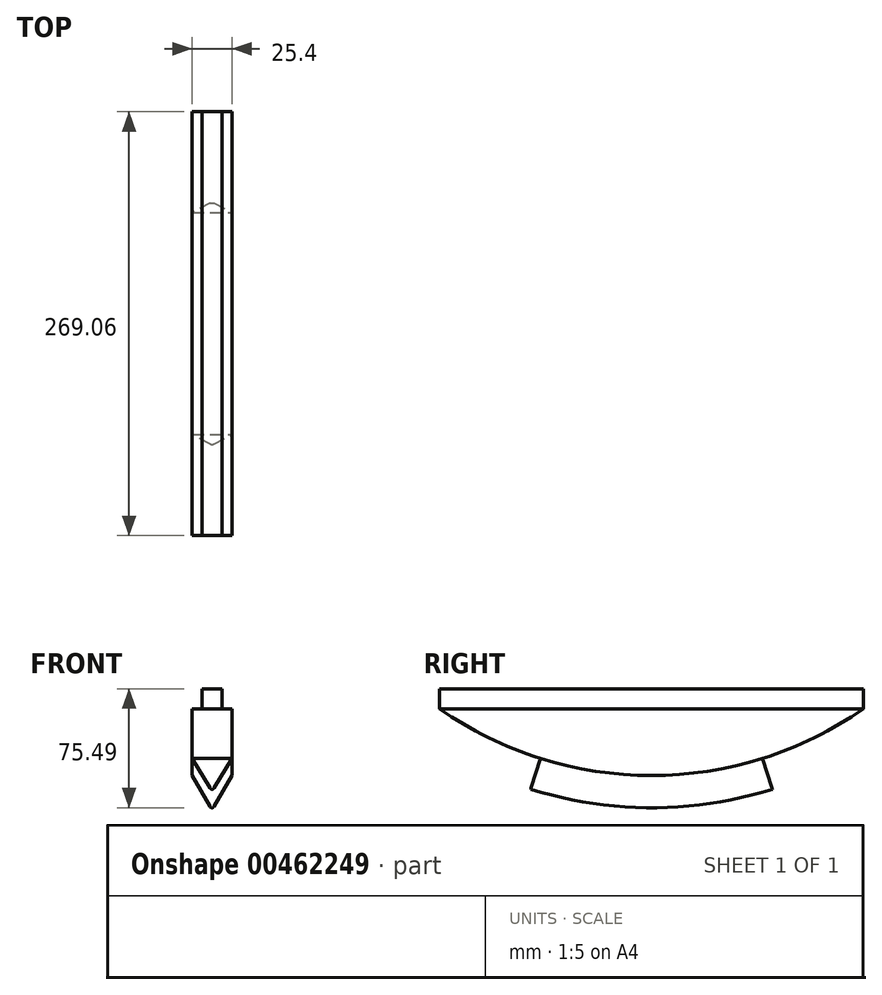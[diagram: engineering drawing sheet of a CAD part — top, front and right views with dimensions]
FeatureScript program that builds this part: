
annotation { "Feature Type Name" : "Feature", "Feature Type Description" : "" }
export const myFeature = defineFeature(function(context is Context, id is Id, definition is map)
    precondition{}
    {
        {
            var Q0;
            Q0=qCreatedBy(makeId("Front.planeOp"),FACE);
            var sketch = newSketch(context, id + "F0", { "sketchPlane" : qUnion([Q0])});
            skLineSegment(sketch, "E0", {"start": v(-1.32, 2.29) * mm, "end": v(-12.7, 22) * mm});
            skLineSegment(sketch, "E1", {"start": v(1.32, 2.29) * mm, "end": v(12.7, 22) * mm});
            skPoint(sketch, "E2.visualSharp", {"position": v(0, 0) * mm});
            skArc(sketch, "E2.filletArc", {"start": v(-1.32, 2.29) * mm, "mid": v(0, 1.52) * mm, "end": v(1.32, 2.29) * mm});
            skLineSegment(sketch, "E3", {"start": v(-12.7, 22) * mm, "end": v(12.7, 22) * mm});
            skSolve(sketch);
        }
        {
            var Q0;
            Q0=qCreatedBy(makeId("Right.planeOp"),FACE);
            var sketch = newSketch(context, id + "F1", { "sketchPlane" : qUnion([Q0])});
            skArc(sketch, "E4", {"start": v(-76.2, 14.75) * mm, "mid": v(0, 3.05) * mm, "end": v(76.2, 14.75) * mm});
            skLineSegment(sketch, "E5", {"start": v(-76.2, 14.75) * mm, "end": v(76.2, 14.75) * mm, "construction": true});
            skPoint(sketch, "E6", {"position": v(0, 14.75) * mm});
            skSolve(sketch);
        }
        {
            var Q0;
            Q0=makeQuery(id+"F0.imprint","IMPRINT",FACE,{"disambiguationData":[TD([[makeQuery(id+"F0.imprint","IMPRINT",EDGE,{"derivedFrom":sQuery(id+"F0.wireOp",EDGE,"E0")}),-1.0]])]});
            var Q1;
            Q1=sQuery(id+"F1.wireOp",EDGE,"E4");
            sweep(context, id + "F2", {"profiles" : qUnion([Q0]), "path" : qUnion([Q1])});
        }
        {
            var Q0;
            Q0=makeQuery(id+"F2.opSweep","SWEPT_BODY",BODY,{"disambiguationData":[OSD([sQuery(id+"F0.wireOp",EDGE,"E0"),sQuery(id+"F0.wireOp",EDGE,"E1"),sQuery(id+"F0.wireOp",EDGE,"E2.filletArc"),sQuery(id+"F0.wireOp",EDGE,"E3"),sQuery(id+"F1.wireOp",EDGE,"E4")])]});
            var Q1;
            Q1=qCreatedBy(makeId("Front.planeOp"),FACE);
            mirror(context, id + "F3", {"operationType" : NewBodyOperationType.ADD, "entities" : qUnion([Q0]), "mirrorPlane" : qUnion([Q1])});
        }
        {
            var Q0;
            Q0=qCreatedBy(makeId("Right.planeOp"),FACE);
            var sketch = newSketch(context, id + "F4", { "sketchPlane" : qUnion([Q0])});
            skArc(sketch, "E7.0", {"start": v(134.53, 64.3) * mm, "mid": v(0, 22) * mm, "end": v(-134.53, 64.3) * mm});
            skLineSegment(sketch, "E8", {"start": v(-134.53, 64.3) * mm, "end": v(134.53, 64.3) * mm});
            skSolve(sketch);
        }
        {
            var Q0;
            Q0 = qSketchRegion(id + "F4", true);
            var Q1;
            Q1=makeQuery(id+"F2.opSweep","CAP_VERTEX",VERTEX,{"disambiguationData":[OSD([sQuery(id+"F0.wireOp",EDGE,"E1"),sQuery(id+"F0.wireOp",EDGE,"E3"),sQuery(id+"F1.wireOp",EDGE,"E4")])],"isStart":false});
            var Q2;
            Q2=makeQuery(id+"F2.opSweep","CAP_VERTEX",VERTEX,{"disambiguationData":[OSD([sQuery(id+"F0.wireOp",EDGE,"E0"),sQuery(id+"F0.wireOp",EDGE,"E3"),sQuery(id+"F1.wireOp",EDGE,"E4")])],"isStart":false});
            extrude(context, id + "F5", {"entities" : qUnion([Q0]), "operationType" : NewBodyOperationType.ADD, "endBound" : BoundingType.UP_TO_VERTEX, "endBoundEntityVertex" : qUnion([Q1]), "depth" : 25.4 * mm, "hasSecondDirection" : true, "secondDirectionBound" : SecondDirectionBoundingType.UP_TO_VERTEX, "secondDirectionOppositeDirection" : true, "secondDirectionBoundEntityVertex" : qUnion([Q2]), "secondDirectionDepth" : 25.4 * mm});
        }
        {
            var Q0;
            Q0=qCreatedBy(makeId("Front.planeOp"),FACE);
            var sketch = newSketch(context, id + "F6", { "sketchPlane" : qUnion([Q0])});
            skLineSegment(sketch, "E9.bottom", {"start": v(-6.35, 64.3) * mm, "end": v(6.35, 64.3) * mm});
            skLineSegment(sketch, "E9.top", {"start": v(-6.35, 77) * mm, "end": v(6.35, 77) * mm});
            skLineSegment(sketch, "E9.left", {"start": v(-6.35, 64.3) * mm, "end": v(-6.35, 77) * mm});
            skLineSegment(sketch, "E9.right", {"start": v(6.35, 64.3) * mm, "end": v(6.35, 77) * mm});
            skSolve(sketch);
        }
        {
            var Q0;
            Q0 = qSketchRegion(id + "F6", true);
            var Q1;
            Q1=makeQuery(id+"F5.boolean.opBoolean","MERGE",VERTEX,{"derivedFrom":[makeQuery(id+"F2.opSweep","CAP_VERTEX",VERTEX,{"disambiguationData":[OSD([sQuery(id+"F0.wireOp",EDGE,"E1"),sQuery(id+"F0.wireOp",EDGE,"E3"),sQuery(id+"F1.wireOp",EDGE,"E4")])],"isStart":false}),makeQuery(id+"F5.opExtrude","CAP_VERTEX",VERTEX,{"disambiguationData":[OSD([sQuery(id+"F4.wireOp",EDGE,"E7.0"),sQuery(id+"F4.wireOp",EDGE,"E8"),dummyQuery(id+"F5.vertexPlane.planeOp",FACE)]),OD(0.0)],"isStart":false})]});
            var Q2;
            Q2=makeQuery(id+"F5.boolean.opBoolean","MERGE",VERTEX,{"derivedFrom":[makeQuery(id+"F3.opPattern","COPY",VERTEX,{"derivedFrom":makeQuery(id+"F2.opSweep","CAP_VERTEX",VERTEX,{"disambiguationData":[OSD([sQuery(id+"F0.wireOp",EDGE,"E1"),sQuery(id+"F0.wireOp",EDGE,"E3"),sQuery(id+"F1.wireOp",EDGE,"E4")])],"isStart":false}),"instanceName":"1"}),makeQuery(id+"F5.opExtrude","CAP_VERTEX",VERTEX,{"disambiguationData":[OSD([sQuery(id+"F4.wireOp",EDGE,"E7.0"),sQuery(id+"F4.wireOp",EDGE,"E8"),dummyQuery(id+"F5.vertexPlane.planeOp",FACE)]),OD(1.0)],"isStart":false})]});
            extrude(context, id + "F7", {"entities" : qUnion([Q0]), "operationType" : NewBodyOperationType.ADD, "endBound" : BoundingType.UP_TO_VERTEX, "endBoundEntityVertex" : qUnion([Q1]), "depth" : 25.4 * mm, "hasSecondDirection" : true, "secondDirectionBound" : SecondDirectionBoundingType.UP_TO_VERTEX, "secondDirectionOppositeDirection" : true, "secondDirectionBoundEntityVertex" : qUnion([Q2]), "secondDirectionDepth" : 25.4 * mm});
        }
    });
